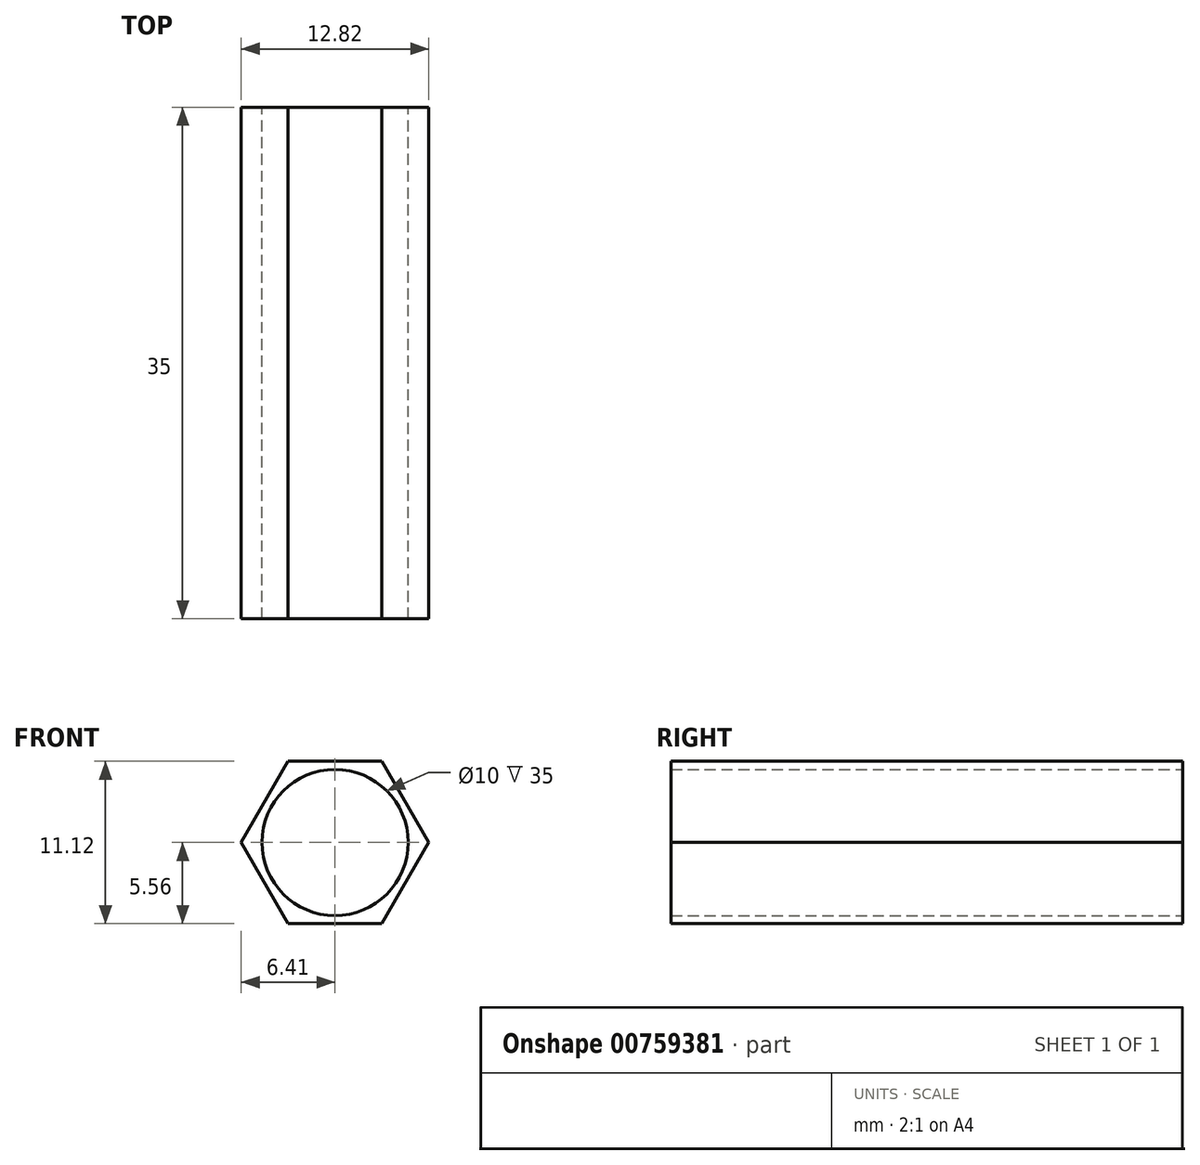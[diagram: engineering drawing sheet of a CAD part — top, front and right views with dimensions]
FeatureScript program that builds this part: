
annotation { "Feature Type Name" : "Feature", "Feature Type Description" : "" }
export const myFeature = defineFeature(function(context is Context, id is Id, definition is map)
    precondition{}
    {
        {
            var Q0;
            Q0=qCreatedBy(makeId("Front.planeOp"),FACE);
            var sketch = newSketch(context, id + "F0", { "sketchPlane" : qUnion([Q0])});
            skCircle(sketch, "E0.cCircle", {"center": v(0, 0) * mm, "radius": 5.56 * mm, "construction": true});
            skLineSegment(sketch, "E0.0", {"start": v(3.2, -5.56) * mm, "end": v(-3.2, -5.56) * mm});
            skLineSegment(sketch, "E0.1", {"start": v(-3.2, -5.56) * mm, "end": v(-6.41, 0) * mm});
            skLineSegment(sketch, "E0.2", {"start": v(-6.41, 0) * mm, "end": v(-3.2, 5.55) * mm});
            skLineSegment(sketch, "E0.3", {"start": v(-3.2, 5.55) * mm, "end": v(3.2, 5.56) * mm});
            skLineSegment(sketch, "E0.4", {"start": v(3.2, 5.56) * mm, "end": v(6.41, 0) * mm});
            skLineSegment(sketch, "E0.5", {"start": v(6.41, 0) * mm, "end": v(3.2, -5.56) * mm});
            skPoint(sketch, "E0.0.midPoint", {"position": v(0, -5.56) * mm});
            skCircle(sketch, "E1", {"center": v(0, 0) * mm, "radius": 5 * mm});
            skSolve(sketch);
        }
        {
            var Q0;
            Q0=makeQuery(id+"F0.imprint","IMPRINT",FACE,{"disambiguationData":[TD([[makeQuery(id+"F0.imprint","IMPRINT",EDGE,{"derivedFrom":sQuery(id+"F0.wireOp",EDGE,"E0.0")}),-1.0]])]});
            extrude(context, id + "F1", {"entities" : qUnion([Q0]), "depth" : 35 * mm, "offsetDistance" : 25 * mm});
        }
    });
